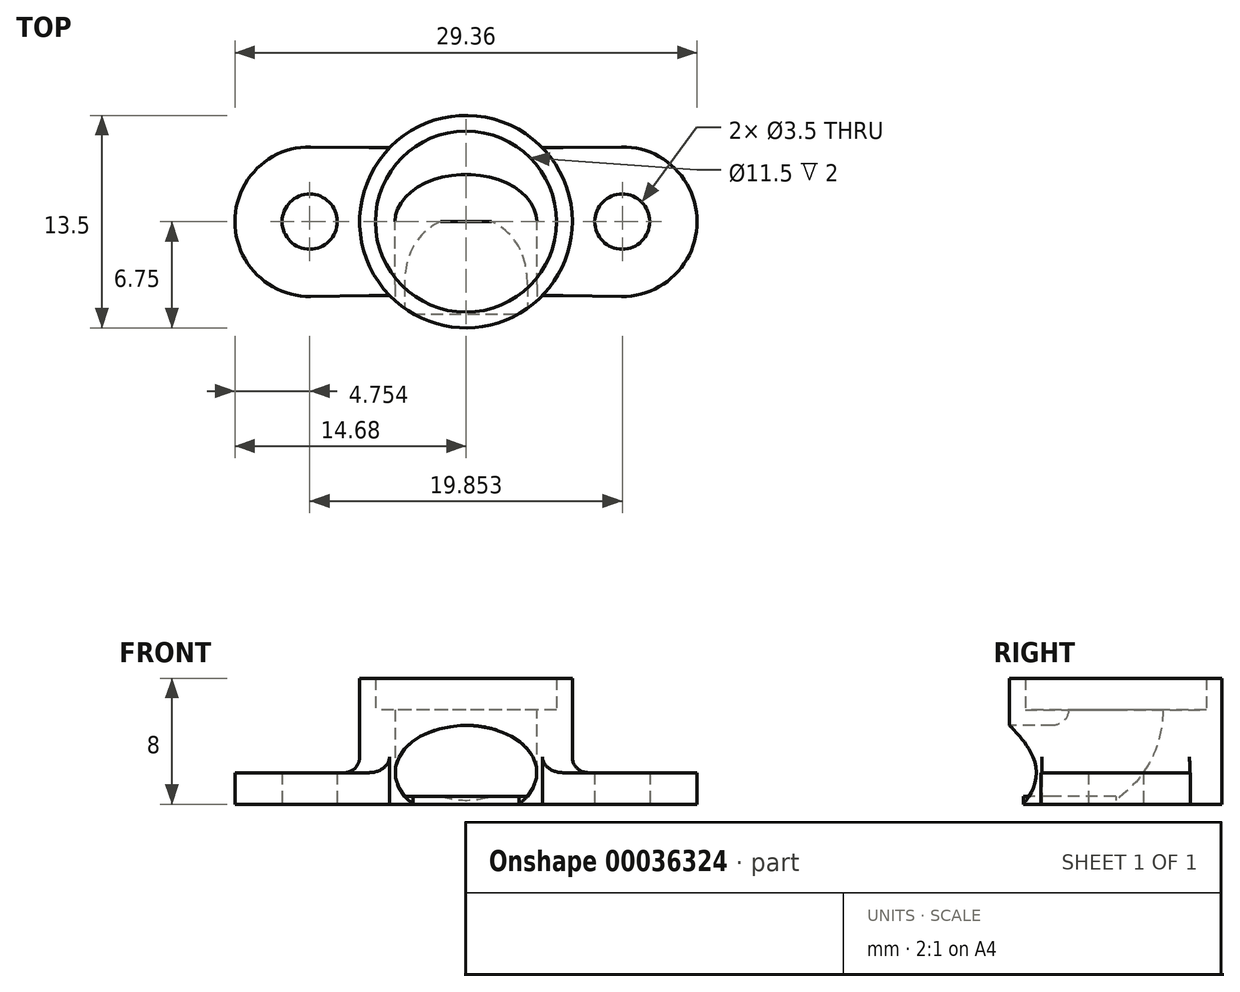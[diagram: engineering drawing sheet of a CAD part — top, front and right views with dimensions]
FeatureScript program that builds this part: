
annotation { "Feature Type Name" : "Feature", "Feature Type Description" : "" }
export const myFeature = defineFeature(function(context is Context, id is Id, definition is map)
    precondition{}
    {
        {
            var Q0;
            Q0=qCreatedBy(makeId("Top.planeOp"),FACE);
            var sketch = newSketch(context, id + "F0", { "sketchPlane" : qUnion([Q0])});
            skCircle(sketch, "E0", {"center": v(0, 0) * mm, "radius": 6.75 * mm});
            skSolve(sketch);
        }
        {
            var Q0;
            Q0 = qSketchRegion(id + "F0", true);
            extrude(context, id + "F1", {"entities" : qUnion([Q0]), "depth" : 6 * mm});
        }
        {
            var Q0;
            Q0=makeQuery(id+"F1.opExtrude","CAP_FACE",FACE,{"disambiguationData":[OSD([sQuery(id+"F0.wireOp",EDGE,"E0")])],"isStart":false});
            var sketch = newSketch(context, id + "F2", { "sketchPlane" : qUnion([Q0])});
            skCircle(sketch, "E1", {"center": v(0, 0) * mm, "radius": 5.75 * mm});
            skCircle(sketch, "E2", {"center": v(0, 0) * mm, "radius": 6.75 * mm});
            skSolve(sketch);
        }
        {
            var Q0;
            Q0=makeQuery(id+"F2.imprint","IMPRINT",FACE,{"disambiguationData":[TD([[makeQuery(id+"F2.imprint","IMPRINT",EDGE,{"derivedFrom":sQuery(id+"F2.wireOp",EDGE,"E1")}),-1.0]])]});
            extrude(context, id + "F3", {"entities" : qUnion([Q0]), "operationType" : NewBodyOperationType.ADD, "depth" : 2 * mm});
        }
        {
            var Q0;
            Q0=qCreatedBy(makeId("Top.planeOp"),FACE);
            var sketch = newSketch(context, id + "F4", { "sketchPlane" : qUnion([Q0])});
            skArc(sketch, "E3", {"start": v(-9.87, 4.75) * mm, "mid": v(-14.68, 0) * mm, "end": v(-9.87, -4.75) * mm});
            skLineSegment(sketch, "E4", {"start": v(0, 5.94) * mm, "end": v(0, -6.04) * mm, "construction": true});
            skCircle(sketch, "E5", {"center": v(-9.93, 0) * mm, "radius": 1.75 * mm});
            skArc(sketch, "E6.MirrorCS", {"start": v(9.87, 4.75) * mm, "mid": v(14.68, 0) * mm, "end": v(9.87, -4.75) * mm});
            skCircle(sketch, "E7.MirrorC", {"center": v(9.93, 0) * mm, "radius": 1.75 * mm});
            skLineSegment(sketch, "E8", {"start": v(-5.5, 0) * mm, "end": v(5.77, 0) * mm, "construction": true});
            skLineSegment(sketch, "E9", {"start": v(-9.87, 4.75) * mm, "end": v(-4.85, 4.7) * mm});
            skLineSegment(sketch, "E10", {"start": v(-9.87, -4.75) * mm, "end": v(-4.85, -4.7) * mm});
            skLineSegment(sketch, "E11", {"start": v(9.87, -4.75) * mm, "end": v(4.85, -4.7) * mm});
            skLineSegment(sketch, "E12", {"start": v(9.87, 4.75) * mm, "end": v(4.85, 4.7) * mm});
            skFitSpline(sketch, "E13", {"points": [v(-4.85, -4.7) * mm, v(-4.85, -4.1) * mm, v(-5.7, -2.48) * mm, v(-6.17, 0) * mm, v(-5.5, 2.99) * mm, v(-4.85, 4.7) * mm], "startDerivative": vector(0.89, 4.78) * mm, "endDerivative": vector(3.16, 7.84) * mm});
            skFitSpline(sketch, "E14", {"points": [v(4.85, 4.7) * mm, v(5.63, 2.47) * mm, v(6.24, -0.23) * mm, v(5.72, -2.67) * mm, v(4.85, -4.7) * mm], "startDerivative": vector(3.1, -8.78) * mm, "endDerivative": vector(-3.8, -8.27) * mm});
            skSolve(sketch);
        }
        {
            var Q0;
            Q0 = qSketchRegion(id + "F4", true);
            extrude(context, id + "F5", {"entities" : qUnion([Q0]), "operationType" : NewBodyOperationType.ADD, "depth" : 2 * mm});
        }
        {
            var Q0;
            Q0=makeQuery(id+"F5.boolean.opBoolean","INTERSECT",EDGE,{"derivedFrom":[makeQuery(id+"F3.boolean.opBoolean","MERGE",FACE,{"derivedFrom":[makeQuery(id+"F1.opExtrude","SWEPT_FACE",FACE,{"disambiguationData":[OSD([sQuery(id+"F0.wireOp",EDGE,"E0")])]}),makeQuery(id+"F3.opExtrude","SWEPT_FACE",FACE,{"disambiguationData":[OSD([sQuery(id+"F2.wireOp",EDGE,"E2")])]})]}),makeQuery(id+"F5.opExtrude","CAP_FACE",FACE,{"disambiguationData":[OSD([sQuery(id+"F4.wireOp",EDGE,"E6.MirrorCS"),sQuery(id+"F4.wireOp",EDGE,"E7.MirrorC"),sQuery(id+"F4.wireOp",EDGE,"E11"),sQuery(id+"F4.wireOp",EDGE,"E12"),sQuery(id+"F4.wireOp",EDGE,"E14")])],"isStart":false})]});
            var Q1;
            Q1=makeQuery(id+"F5.opExtrude","SWEPT_EDGE",EDGE,{"disambiguationData":[OSD([sQuery(id+"F4.wireOp",EDGE,"E11"),sQuery(id+"F4.wireOp",EDGE,"E14")])]});
            var Q2;
            Q2=makeQuery(id+"F5.opExtrude","SWEPT_EDGE",EDGE,{"disambiguationData":[OSD([sQuery(id+"F4.wireOp",EDGE,"E12"),sQuery(id+"F4.wireOp",EDGE,"E14")])]});
            var Q3;
            Q3=makeQuery(id+"F5.opExtrude","SWEPT_EDGE",EDGE,{"disambiguationData":[OSD([sQuery(id+"F4.wireOp",EDGE,"E9"),sQuery(id+"F4.wireOp",EDGE,"E13")])]});
            var Q4;
            Q4=makeQuery(id+"F5.boolean.opBoolean","INTERSECT",EDGE,{"derivedFrom":[makeQuery(id+"F3.boolean.opBoolean","MERGE",FACE,{"derivedFrom":[makeQuery(id+"F1.opExtrude","SWEPT_FACE",FACE,{"disambiguationData":[OSD([sQuery(id+"F0.wireOp",EDGE,"E0")])]}),makeQuery(id+"F3.opExtrude","SWEPT_FACE",FACE,{"disambiguationData":[OSD([sQuery(id+"F2.wireOp",EDGE,"E2")])]})]}),makeQuery(id+"F5.opExtrude","CAP_FACE",FACE,{"disambiguationData":[OSD([sQuery(id+"F4.wireOp",EDGE,"E3"),sQuery(id+"F4.wireOp",EDGE,"E5"),sQuery(id+"F4.wireOp",EDGE,"E9"),sQuery(id+"F4.wireOp",EDGE,"E10"),sQuery(id+"F4.wireOp",EDGE,"E13")])],"isStart":false})]});
            var Q5;
            Q5=makeQuery(id+"F5.opExtrude","SWEPT_EDGE",EDGE,{"disambiguationData":[OSD([sQuery(id+"F4.wireOp",EDGE,"E10"),sQuery(id+"F4.wireOp",EDGE,"E13")])]});
            fillet(context, id + "F6", {"entities" : qUnion([Q0, Q1, Q2, Q3, Q4, Q5]), "radius" : 1 * mm, "tangentPropagation" : true, "allowEdgeOverflow" : false});
        }
        {
            var Q0;
            Q0=makeQuery(id+"F1.opExtrude","CAP_FACE",FACE,{"disambiguationData":[OSD([sQuery(id+"F0.wireOp",EDGE,"E0")])],"isStart":false});
            var sketch = newSketch(context, id + "F7", { "sketchPlane" : qUnion([Q0])});
            skEllipse(sketch, "E15", {"center": v(0, 0) * mm, "majorRadius": 4.5 * mm, "minorRadius": 3 * mm, "majorAxis": v(1, 0)});
            skSolve(sketch);
        }
        {
            var Q0;
            Q0=qCreatedBy(makeId("Right.planeOp"),FACE);
            var sketch = newSketch(context, id + "F8", { "sketchPlane" : qUnion([Q0])});
            skLineSegment(sketch, "E16", {"start": v(0, 6) * mm, "end": v(0, 6) * mm});
            skLineSegment(sketch, "E17", {"start": v(-4, 2) * mm, "end": v(-9.96, 2) * mm});
            skPoint(sketch, "E18.visualSharp", {"position": v(0, 2) * mm});
            skArc(sketch, "E18.filletArc", {"start": v(-4, 2) * mm, "mid": v(-1.17, 3.17) * mm, "end": v(0, 6) * mm});
            skSolve(sketch);
        }
        {
            var Q0;
            Q0 = qSketchRegion(id + "F7", true);
            var Q1;
            Q1 = qConstructionFilter(qBodyType(qCreatedBy(id + "F8" ,EDGE), BodyType.WIRE), ConstructionObject.NO);
            sweep(context, id + "F9", {"operationType" : NewBodyOperationType.REMOVE, "profiles" : qUnion([Q0]), "path" : qUnion([Q1])});
        }
        {
            var Q0;
            Q0=makeQuery(id+"F5.boolean.opBoolean","MERGE",FACE,{"derivedFrom":[makeQuery(id+"F1.opExtrude","CAP_FACE",FACE,{"disambiguationData":[OSD([sQuery(id+"F0.wireOp",EDGE,"E0")])],"isStart":true}),makeQuery(id+"F5.opExtrude","CAP_FACE",FACE,{"disambiguationData":[OSD([sQuery(id+"F4.wireOp",EDGE,"E3"),sQuery(id+"F4.wireOp",EDGE,"E5"),sQuery(id+"F4.wireOp",EDGE,"E9"),sQuery(id+"F4.wireOp",EDGE,"E10"),sQuery(id+"F4.wireOp",EDGE,"E13")])],"isStart":true}),makeQuery(id+"F5.opExtrude","CAP_FACE",FACE,{"disambiguationData":[OSD([sQuery(id+"F4.wireOp",EDGE,"E6.MirrorCS"),sQuery(id+"F4.wireOp",EDGE,"E7.MirrorC"),sQuery(id+"F4.wireOp",EDGE,"E11"),sQuery(id+"F4.wireOp",EDGE,"E12"),sQuery(id+"F4.wireOp",EDGE,"E14")])],"isStart":true})]});
            var sketch = newSketch(context, id + "F10", { "sketchPlane" : qUnion([Q0])});
            skLineSegment(sketch, "E19.bottom", {"start": v(-4, 0) * mm, "end": v(4, 0) * mm});
            skLineSegment(sketch, "E19.left", {"start": v(-4, 0) * mm, "end": v(-4, 5.44) * mm});
            skLineSegment(sketch, "E19.right", {"start": v(4, 0) * mm, "end": v(4, 5.44) * mm});
            skLineSegment(sketch, "E20", {"start": v(-4, 5.44) * mm, "end": v(-3.35, 5.86) * mm});
            skLineSegment(sketch, "E21", {"start": v(-3.35, 5.86) * mm, "end": v(3.35, 5.86) * mm});
            skLineSegment(sketch, "E22", {"start": v(3.35, 5.86) * mm, "end": v(4, 5.44) * mm});
            skSolve(sketch);
        }
        {
            var Q0;
            Q0 = qSketchRegion(id + "F10", true);
            extrude(context, id + "F11", {"entities" : qUnion([Q0]), "operationType" : NewBodyOperationType.ADD, "oppositeDirection" : true, "depth" : .5 * mm});
        }
    });
